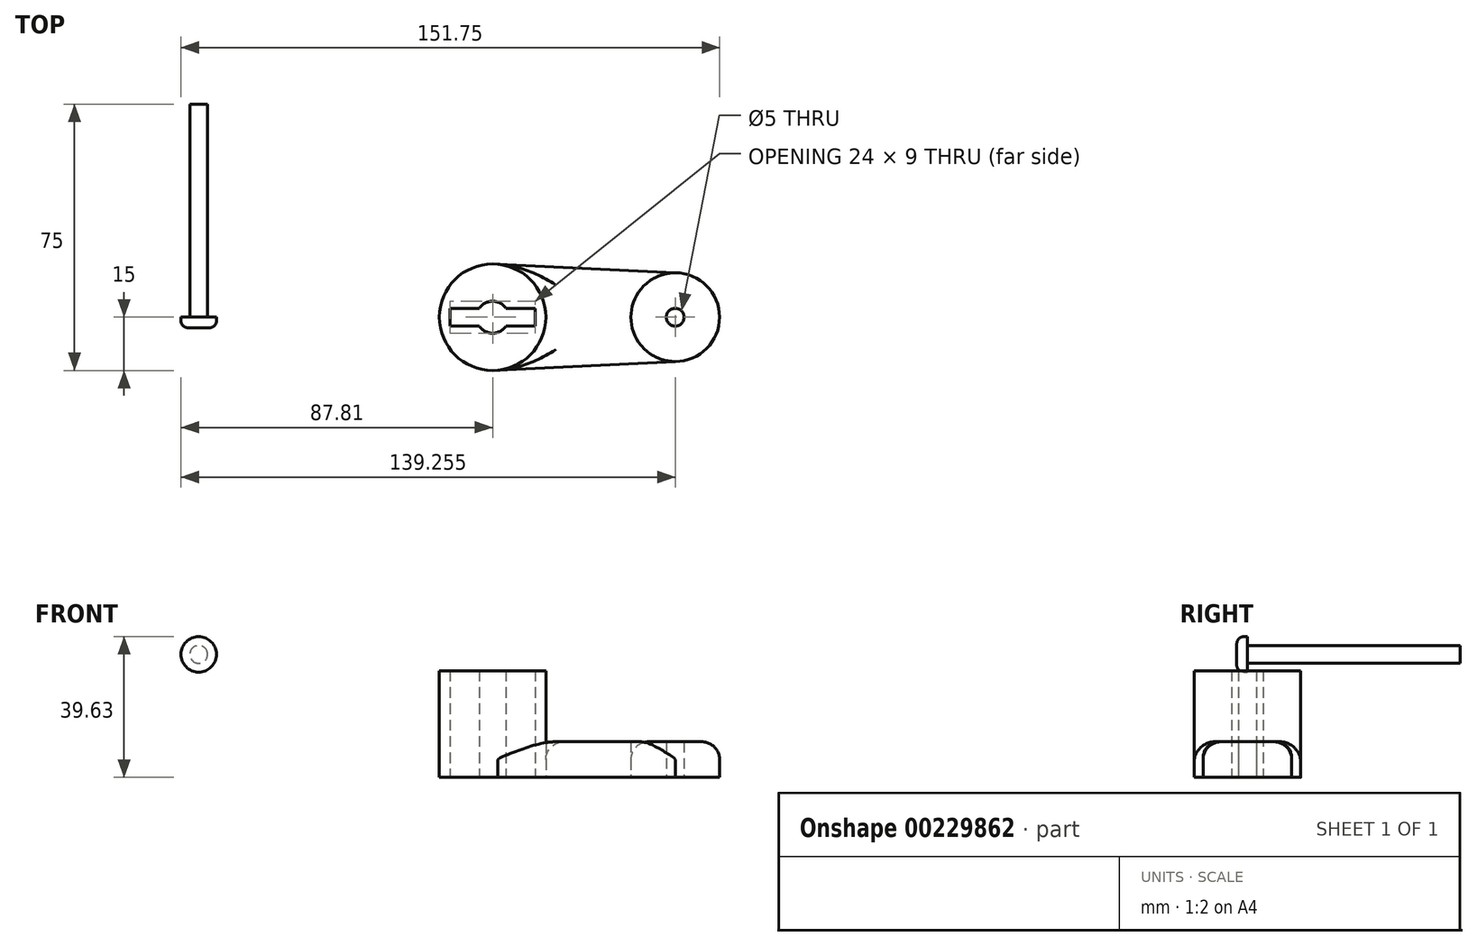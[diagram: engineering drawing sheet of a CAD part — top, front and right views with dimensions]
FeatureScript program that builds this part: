
annotation { "Feature Type Name" : "Feature", "Feature Type Description" : "" }
export const myFeature = defineFeature(function(context is Context, id is Id, definition is map)
    precondition{}
    {
        {
            var Q0;
            Q0=qCreatedBy(makeId("Top.planeOp"),FACE);
            var sketch = newSketch(context, id + "F0", { "sketchPlane" : qUnion([Q0])});
            skCircle(sketch, "E0", {"center": v(0, 0) * mm, "radius": 4.5 * mm});
            skCircle(sketch, "E1", {"center": v(0, 0) * mm, "radius": 15 * mm});
            skLineSegment(sketch, "E2", {"start": v(0, 0) * mm, "end": v(-12, 0) * mm});
            skLineSegment(sketch, "E3", {"start": v(0, 0) * mm, "end": v(12, 0) * mm});
            skLineSegment(sketch, "E4", {"start": v(-12, 0) * mm, "end": v(-12, 2.5) * mm});
            skLineSegment(sketch, "E5", {"start": v(-12, 0) * mm, "end": v(-12, -2.5) * mm});
            skLineSegment(sketch, "E6", {"start": v(12, 2.5) * mm, "end": v(12, -2.5) * mm});
            skLineSegment(sketch, "E7", {"start": v(-12, 2.5) * mm, "end": v(12, 2.5) * mm});
            skLineSegment(sketch, "E8", {"start": v(12, -2.5) * mm, "end": v(-12, -2.5) * mm});
            skSolve(sketch);
        }
        {
            var Q0;
            Q0=makeQuery(id+"F0.imprint","IMPRINT",FACE,{"disambiguationData":[TD([[makeQuery(id+"F0.imprint","IMPRINT",EDGE,{"derivedFrom":sQuery(id+"F0.wireOp",EDGE,"E1")}),1.0]])]});
            extrude(context, id + "F1", {"entities" : qUnion([Q0]), "depth" : 30 * mm});
        }
        {
            var Q0;
            Q0=makeQuery(id+"F1.opExtrude","CAP_FACE",FACE,{"disambiguationData":[OSD([sQuery(id+"F0.wireOp",EDGE,"E0"),sQuery(id+"F0.wireOp",EDGE,"E1"),sQuery(id+"F0.wireOp",EDGE,"E4"),sQuery(id+"F0.wireOp",EDGE,"E5"),sQuery(id+"F0.wireOp",EDGE,"E6"),sQuery(id+"F0.wireOp",EDGE,"E7"),sQuery(id+"F0.wireOp",EDGE,"E8")])],"isStart":true});
            var sketch = newSketch(context, id + "F2", { "sketchPlane" : qUnion([Q0])});
            skCircle(sketch, "E9.0", {"center": v(0, 0) * mm, "radius": 15 * mm});
            skPoint(sketch, "E10", {"position": v(0, 15) * mm});
            skPoint(sketch, "E10.positionSnap0", {"position": v(0, 4.5) * mm});
            skPoint(sketch, "E11", {"position": v(0, -15) * mm});
            skCircle(sketch, "E12", {"center": v(51.44, 0) * mm, "radius": 12.5 * mm});
            skCircle(sketch, "E13", {"center": v(51.44, 0) * mm, "radius": 2.5 * mm});
            skSolve(sketch);
        }
        {
            var Q0;
            Q0=makeQuery(id+"F2.imprint","IMPRINT",FACE,{"disambiguationData":[TD([[makeQuery(id+"F2.imprint","IMPRINT",EDGE,{"derivedFrom":sQuery(id+"F2.wireOp",EDGE,"E12")}),1.0]])]});
            extrude(context, id + "F3", {"entities" : qUnion([Q0]), "oppositeDirection" : true, "depth" : 10 * mm});
        }
        {
            var Q0;
            Q0=makeQuery(id+"F1.opExtrude","CAP_FACE",FACE,{"disambiguationData":[OSD([sQuery(id+"F0.wireOp",EDGE,"E0"),sQuery(id+"F0.wireOp",EDGE,"E1"),sQuery(id+"F0.wireOp",EDGE,"E4"),sQuery(id+"F0.wireOp",EDGE,"E5"),sQuery(id+"F0.wireOp",EDGE,"E6"),sQuery(id+"F0.wireOp",EDGE,"E7"),sQuery(id+"F0.wireOp",EDGE,"E8")])],"isStart":true});
            var sketch = newSketch(context, id + "F4", { "sketchPlane" : qUnion([Q0])});
            skPoint(sketch, "E14", {"position": v(0, 15) * mm});
            skPoint(sketch, "E14.positionSnap0", {"position": v(0, 4.5) * mm});
            skPoint(sketch, "E15", {"position": v(0, -15) * mm});
            skCircle(sketch, "E16.0", {"center": v(51.44, 0) * mm, "radius": 12.5 * mm});
            skPoint(sketch, "E17", {"position": v(51.44, 12.5) * mm});
            skPoint(sketch, "E18", {"position": v(51.44, -12.5) * mm});
            skLineSegment(sketch, "E19", {"start": v(0, 15) * mm, "end": v(51.44, 12.5) * mm});
            skLineSegment(sketch, "E20", {"start": v(51.44, -12.5) * mm, "end": v(0, -15) * mm});
            skSolve(sketch);
        }
        {
            var Q0;
            {var subQ0=sQuery(id+"F4.wireOp",EDGE,"E19");var subQ1=sQuery(id+"F4.wireOp",EDGE,"E16.0");var subQ2=makeQuery(id+"F4.imprint","INTERSECT",VERTEX,{"derivedFrom":[subQ1,subQ0]});Q0=makeQuery(id+"F4.imprint","IMPRINT",FACE,{"disambiguationData":[TD([[makeQuery(id+"F4.imprint","IMPRINT",EDGE,{"disambiguationData":[TD([[subQ2,-1.0]])],"derivedFrom":subQ1}),-1.0]])]});}
            extrude(context, id + "F5", {"entities" : qUnion([Q0]), "oppositeDirection" : true, "depth" : 10 * mm});
        }
        {
            var Q0;
            Q0=makeQuery(id+"F3.opExtrude","CAP_EDGE",EDGE,{"disambiguationData":[OSD([sQuery(id+"F2.wireOp",EDGE,"E12")])],"isStart":false});
            var Q1;
            Q1=makeQuery(id+"F5.opExtrude","CAP_EDGE",EDGE,{"disambiguationData":[OSD([sQuery(id+"F4.wireOp",EDGE,"E20")])],"isStart":false});
            var Q2;
            Q2=makeQuery(id+"F5.opExtrude","CAP_EDGE",EDGE,{"disambiguationData":[OSD([sQuery(id+"F4.wireOp",EDGE,"E19")])],"isStart":false});
            var Q3;
            Q3=makeQuery(id+"F5.opExtrude","CAP_EDGE",EDGE,{"disambiguationData":[OSD([sQuery(id+"F0.wireOp",EDGE,"E1")])],"isStart":false});
            fillet(context, id + "F6", {"entities" : qUnion([Q0, Q1, Q2, Q3]), "radius" : 5 * mm, "tangentPropagation" : true, "allowEdgeOverflow" : false});
        }
        {
            var Q0;
            Q0=qCreatedBy(makeId("Front.planeOp"),FACE);
            var sketch = newSketch(context, id + "F7", { "sketchPlane" : qUnion([Q0])});
            skCircle(sketch, "E21", {"center": v(-82.81, 34.63) * mm, "radius": 2.5 * mm});
            skCircle(sketch, "E22", {"center": v(-82.81, 34.63) * mm, "radius": 5 * mm});
            skSolve(sketch);
        }
        {
            var Q0;
            Q0=makeQuery(id+"F7.imprint","IMPRINT",FACE,{"disambiguationData":[TD([[makeQuery(id+"F7.imprint","IMPRINT",EDGE,{"derivedFrom":sQuery(id+"F7.wireOp",EDGE,"E21")}),1.0]])]});
            extrude(context, id + "F8", {"entities" : qUnion([Q0]), "oppositeDirection" : true, "depth" : 60 * mm});
        }
        {
            var Q0;
            Q0=makeQuery(id+"F7.imprint","IMPRINT",FACE,{"disambiguationData":[TD([[makeQuery(id+"F7.imprint","IMPRINT",EDGE,{"derivedFrom":sQuery(id+"F7.wireOp",EDGE,"E21")}),-1.0]])]});
            var Q1;
            Q1=makeQuery(id+"F7.imprint","IMPRINT",FACE,{"disambiguationData":[TD([[makeQuery(id+"F7.imprint","IMPRINT",EDGE,{"derivedFrom":sQuery(id+"F7.wireOp",EDGE,"E21")}),1.0]])]});
            extrude(context, id + "F9", {"entities" : qUnion([Q0, Q1]), "operationType" : NewBodyOperationType.ADD, "depth" : 3 * mm});
        }
        {
            var Q0;
            Q0=makeQuery(id+"F9.opExtrude","CAP_EDGE",EDGE,{"disambiguationData":[OSD([sQuery(id+"F7.wireOp",EDGE,"E22")])],"isStart":false});
            fillet(context, id + "F10", {"entities" : qUnion([Q0]), "radius" : 2 * mm, "tangentPropagation" : true, "allowEdgeOverflow" : false});
        }
    });
